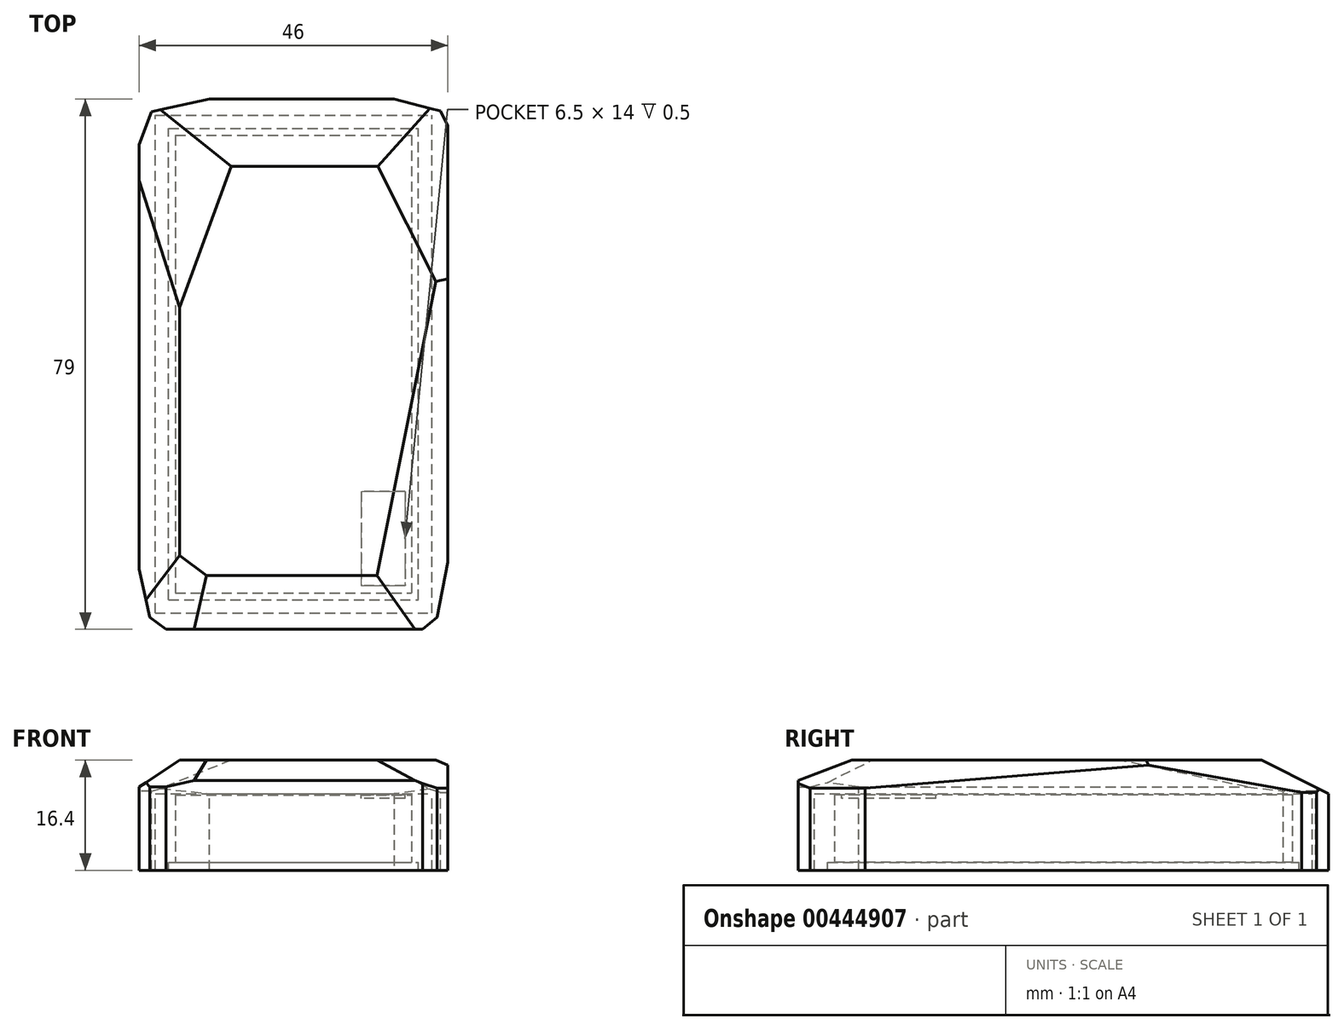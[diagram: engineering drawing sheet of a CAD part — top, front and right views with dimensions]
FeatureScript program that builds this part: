
annotation { "Feature Type Name" : "Feature", "Feature Type Description" : "" }
export const myFeature = defineFeature(function(context is Context, id is Id, definition is map)
    precondition{}
    {
        {
            var Q0;
            Q0=qCreatedBy(makeId("Top.planeOp"),FACE);
            var sketch = newSketch(context, id + "F0", { "sketchPlane" : qUnion([Q0])});
            skLineSegment(sketch, "E0.bottom", {"start": v(-17.6, 34.1) * mm, "end": v(17.6, 34.1) * mm});
            skLineSegment(sketch, "E0.top", {"start": v(-17.6, -34.1) * mm, "end": v(17.6, -34.1) * mm});
            skLineSegment(sketch, "E0.left", {"start": v(-17.6, 34.1) * mm, "end": v(-17.6, -34.1) * mm});
            skLineSegment(sketch, "E0.right", {"start": v(17.6, 34.1) * mm, "end": v(17.6, -34.1) * mm});
            skPoint(sketch, "E0.middle", {"position": v(0, 0) * mm});
            skSolve(sketch);
        }
        {
            var Q0;
            Q0=makeQuery(id+"F0.imprint","IMPRINT",FACE,{"disambiguationData":[TD([[makeQuery(id+"F0.imprint","IMPRINT",EDGE,{"derivedFrom":sQuery(id+"F0.wireOp",EDGE,"E0.bottom")}),-1.0]])]});
            extrude(context, id + "F1", {"entities" : qUnion([Q0]), "depth" : 10 * mm});
        }
        {
            var Q0;
            Q0=makeQuery(id+"F1.opExtrude","CAP_FACE",FACE,{"disambiguationData":[OSD([sQuery(id+"F0.wireOp",EDGE,"E0.bottom"),sQuery(id+"F0.wireOp",EDGE,"E0.top"),sQuery(id+"F0.wireOp",EDGE,"E0.left"),sQuery(id+"F0.wireOp",EDGE,"E0.right")])],"isStart":false});
            var sketch = newSketch(context, id + "F2", { "sketchPlane" : qUnion([Q0])});
            skLineSegment(sketch, "E1.bottom", {"start": v(16.6, -19) * mm, "end": v(10.1, -19) * mm});
            skLineSegment(sketch, "E1.top", {"start": v(16.6, -33) * mm, "end": v(10.1, -33) * mm});
            skLineSegment(sketch, "E1.left", {"start": v(16.6, -19) * mm, "end": v(16.6, -33) * mm});
            skLineSegment(sketch, "E1.right", {"start": v(10.1, -19) * mm, "end": v(10.1, -33) * mm});
            skPoint(sketch, "E1.middle", {"position": v(13.35, -26) * mm});
            skSolve(sketch);
        }
        {
            var Q0;
            Q0=qSketchRegion(id+"F2",true);
            extrude(context, id + "F3", {"entities" : qUnion([Q0]), "operationType" : NewBodyOperationType.REMOVE, "oppositeDirection" : true, "depth" : 0.5 * mm});
        }
        {
            var Q0;
            Q0=makeQuery(id+"F1.opExtrude","CAP_FACE",FACE,{"disambiguationData":[OSD([sQuery(id+"F0.wireOp",EDGE,"E0.bottom"),sQuery(id+"F0.wireOp",EDGE,"E0.top"),sQuery(id+"F0.wireOp",EDGE,"E0.left"),sQuery(id+"F0.wireOp",EDGE,"E0.right")])],"isStart":true});
            var sketch = newSketch(context, id + "F4", { "sketchPlane" : qUnion([Q0])});
            skLineSegment(sketch, "E2.bottom", {"start": v(-18.6, 35.1) * mm, "end": v(18.6, 35.1) * mm});
            skLineSegment(sketch, "E2.top", {"start": v(-18.6, -35.1) * mm, "end": v(18.6, -35.1) * mm});
            skLineSegment(sketch, "E2.left", {"start": v(-18.6, 35.1) * mm, "end": v(-18.6, -35.1) * mm});
            skLineSegment(sketch, "E2.right", {"start": v(18.6, 35.1) * mm, "end": v(18.6, -35.1) * mm});
            skPoint(sketch, "E2.middle", {"position": v(0, 0) * mm});
            skSolve(sketch);
        }
        {
            var Q0;
            Q0=qSketchRegion(id+"F4",true);
            extrude(context, id + "F5", {"entities" : qUnion([Q0]), "depth" : 1.2 * mm});
        }
        {
            var Q0;
            Q0=makeQuery(id+"F1.opExtrude","CAP_FACE",FACE,{"disambiguationData":[OSD([sQuery(id+"F0.wireOp",EDGE,"E0.bottom"),sQuery(id+"F0.wireOp",EDGE,"E0.top"),sQuery(id+"F0.wireOp",EDGE,"E0.left"),sQuery(id+"F0.wireOp",EDGE,"E0.right")])],"isStart":false});
            var sketch = newSketch(context, id + "F6", { "sketchPlane" : qUnion([Q0])});
            skLineSegment(sketch, "E3.0", {"start": v(-20.6, 37.1) * mm, "end": v(20.6, 37.1) * mm});
            skLineSegment(sketch, "E3.1", {"start": v(-20.6, -37.1) * mm, "end": v(-20.6, 37.1) * mm});
            skLineSegment(sketch, "E3.2", {"start": v(-20.6, -37.1) * mm, "end": v(20.6, -37.1) * mm});
            skLineSegment(sketch, "E3.3", {"start": v(20.6, -37.1) * mm, "end": v(20.6, 37.1) * mm});
            skLineSegment(sketch, "E4.0", {"start": v(-23, 39.5) * mm, "end": v(23, 39.5) * mm});
            skLineSegment(sketch, "E4.1", {"start": v(-23, -39.5) * mm, "end": v(-23, 39.5) * mm});
            skLineSegment(sketch, "E4.2", {"start": v(-23, -39.5) * mm, "end": v(23, -39.5) * mm});
            skLineSegment(sketch, "E4.3", {"start": v(23, -39.5) * mm, "end": v(23, 39.5) * mm});
            skSolve(sketch);
        }
        {
            var Q0;
            Q0=qSketchRegion(id+"F6",true);
            var Q1;
            Q1=makeQuery(id+"F5.opExtrude","CAP_FACE",FACE,{"disambiguationData":[OSD([sQuery(id+"F4.wireOp",EDGE,"E2.bottom"),sQuery(id+"F4.wireOp",EDGE,"E2.top"),sQuery(id+"F4.wireOp",EDGE,"E2.left"),sQuery(id+"F4.wireOp",EDGE,"E2.right")])],"isStart":false});
            extrude(context, id + "F7", {"entities" : qUnion([Q0]), "endBound" : BoundingType.UP_TO_SURFACE, "oppositeDirection" : true, "endBoundEntityFace" : qUnion([Q1]), "depth" : 25 * mm, "hasSecondDirection" : true, "secondDirectionOppositeDirection" : false, "secondDirectionDepth" : 0.2 * mm});
        }
        {
            var Q0;
            Q0=makeQuery(id+"F7.opExtrude","CAP_FACE",FACE,{"disambiguationData":[OSD([sQuery(id+"F6.wireOp",EDGE,"E3.0"),sQuery(id+"F6.wireOp",EDGE,"E3.1"),sQuery(id+"F6.wireOp",EDGE,"E3.2"),sQuery(id+"F6.wireOp",EDGE,"E3.3"),sQuery(id+"F6.wireOp",EDGE,"E4.0"),sQuery(id+"F6.wireOp",EDGE,"E4.1"),sQuery(id+"F6.wireOp",EDGE,"E4.2"),sQuery(id+"F6.wireOp",EDGE,"E4.3")])],"isStart":true});
            var sketch = newSketch(context, id + "F8", { "sketchPlane" : qUnion([Q0])});
            skLineSegment(sketch, "E5.0.0", {"start": v(-23, -39.5) * mm, "end": v(23, -39.5) * mm});
            skLineSegment(sketch, "E5.0.1", {"start": v(23, -39.5) * mm, "end": v(23, 39.5) * mm});
            skLineSegment(sketch, "E5.0.2", {"start": v(23, 39.5) * mm, "end": v(-23, 39.5) * mm});
            skLineSegment(sketch, "E5.0.3", {"start": v(-23, 39.5) * mm, "end": v(-23, -39.5) * mm});
            skSolve(sketch);
        }
        {
            var Q0;
            Q0=qSketchRegion(id+"F8",true);
            extrude(context, id + "F9", {"entities" : qUnion([Q0]), "operationType" : NewBodyOperationType.ADD, "depth" : 5 * mm});
        }
        {
            var Q0;
            Q0=makeQuery(id+"F9.boolean.opBoolean","MERGE",EDGE,{"derivedFrom":[makeQuery(id+"F7.opExtrude","SWEPT_EDGE",EDGE,{"disambiguationData":[OSD([sQuery(id+"F6.wireOp",EDGE,"E4.2"),sQuery(id+"F6.wireOp",EDGE,"E4.3")])]}),makeQuery(id+"F9.opExtrude","SWEPT_EDGE",EDGE,{"disambiguationData":[OSD([sQuery(id+"F8.wireOp",EDGE,"E5.0.0"),sQuery(id+"F8.wireOp",EDGE,"E5.0.1")])]})]});
            chamfer(context, id + "F10", {"entities" : qUnion([Q0]), "chamferType" : ChamferType.TWO_OFFSETS, "width1" : 2 * mm, "oppositeDirection" : false, "width2" : 10 * mm, "tangentPropagation" : true});
        }
        {
            var Q0;
            Q0=makeQuery(id+"F9.boolean.opBoolean","MERGE",EDGE,{"derivedFrom":[makeQuery(id+"F7.opExtrude","SWEPT_EDGE",EDGE,{"disambiguationData":[OSD([sQuery(id+"F6.wireOp",EDGE,"E4.1"),sQuery(id+"F6.wireOp",EDGE,"E4.2")])]}),makeQuery(id+"F9.opExtrude","SWEPT_EDGE",EDGE,{"disambiguationData":[OSD([sQuery(id+"F8.wireOp",EDGE,"E5.0.0"),sQuery(id+"F8.wireOp",EDGE,"E5.0.3")])]})]});
            chamfer(context, id + "F11", {"entities" : qUnion([Q0]), "chamferType" : ChamferType.TWO_OFFSETS, "width1" : 3 * mm, "oppositeDirection" : false, "width2" : 4 * mm, "tangentPropagation" : true});
        }
        {
            var Q0;
            Q0=makeQuery(id+"F9.boolean.opBoolean","MERGE",EDGE,{"derivedFrom":[makeQuery(id+"F7.opExtrude","SWEPT_EDGE",EDGE,{"disambiguationData":[OSD([sQuery(id+"F6.wireOp",EDGE,"E4.0"),sQuery(id+"F6.wireOp",EDGE,"E4.1")])]}),makeQuery(id+"F9.opExtrude","SWEPT_EDGE",EDGE,{"disambiguationData":[OSD([sQuery(id+"F8.wireOp",EDGE,"E5.0.2"),sQuery(id+"F8.wireOp",EDGE,"E5.0.3")])]})]});
            chamfer(context, id + "F12", {"entities" : qUnion([Q0]), "chamferType" : ChamferType.TWO_OFFSETS, "width1" : 2.5 * mm, "oppositeDirection" : false, "width2" : 6.8 * mm, "tangentPropagation" : true});
        }
        {
            var Q0;
            Q0=makeQuery(id+"F9.boolean.opBoolean","MERGE",EDGE,{"derivedFrom":[makeQuery(id+"F7.opExtrude","SWEPT_EDGE",EDGE,{"disambiguationData":[OSD([sQuery(id+"F6.wireOp",EDGE,"E4.0"),sQuery(id+"F6.wireOp",EDGE,"E4.3")])]}),makeQuery(id+"F9.opExtrude","SWEPT_EDGE",EDGE,{"disambiguationData":[OSD([sQuery(id+"F8.wireOp",EDGE,"E5.0.1"),sQuery(id+"F8.wireOp",EDGE,"E5.0.2")])]})]});
            chamfer(context, id + "F13", {"entities" : qUnion([Q0]), "chamferType" : ChamferType.TWO_OFFSETS, "width1" : 4 * mm, "oppositeDirection" : false, "width2" : 2 * mm, "tangentPropagation" : true});
        }
        {
            var Q0;
            {var subQ0=sQuery(id+"F8.wireOp",EDGE,"E5.0.3");var subQ1=sQuery(id+"F8.wireOp",EDGE,"E5.0.2");Q0=makeQuery(id+"F12.opChamfer","BLEND_EDGE",EDGE,{"blendedFrom":[makeQuery(id+"F9.boolean.opBoolean","MERGE",EDGE,{"derivedFrom":[makeQuery(id+"F7.opExtrude","SWEPT_EDGE",EDGE,{"disambiguationData":[OSD([sQuery(id+"F6.wireOp",EDGE,"E4.0"),sQuery(id+"F6.wireOp",EDGE,"E4.1")])]}),makeQuery(id+"F9.opExtrude","SWEPT_EDGE",EDGE,{"disambiguationData":[OSD([subQ1,subQ0])]})]}),makeQuery(id+"F9.opExtrude","CAP_FACE",FACE,{"disambiguationData":[OSD([sQuery(id+"F8.wireOp",EDGE,"E5.0.0"),sQuery(id+"F8.wireOp",EDGE,"E5.0.1"),subQ1,subQ0])],"isStart":false})],"blendedInto":[makeQuery(id+"F9.opExtrude","CAP_FACE",FACE,{"disambiguationData":[OSD([sQuery(id+"F8.wireOp",EDGE,"E5.0.0"),sQuery(id+"F8.wireOp",EDGE,"E5.0.1"),subQ1,subQ0])],"isStart":false})]});}
            chamfer(context, id + "F14", {"entities" : qUnion([Q0]), "chamferType" : ChamferType.TWO_OFFSETS, "width1" : 14 * mm, "oppositeDirection" : false, "width2" : 4.6 * mm, "tangentPropagation" : true});
        }
        {
            var Q0;
            {var subQ0=sQuery(id+"F8.wireOp",EDGE,"E5.0.3");var subQ1=sQuery(id+"F8.wireOp",EDGE,"E5.0.0");Q0=makeQuery(id+"F11.opChamfer","BLEND_EDGE",EDGE,{"blendedFrom":[makeQuery(id+"F9.boolean.opBoolean","MERGE",EDGE,{"derivedFrom":[makeQuery(id+"F7.opExtrude","SWEPT_EDGE",EDGE,{"disambiguationData":[OSD([sQuery(id+"F6.wireOp",EDGE,"E4.1"),sQuery(id+"F6.wireOp",EDGE,"E4.2")])]}),makeQuery(id+"F9.opExtrude","SWEPT_EDGE",EDGE,{"disambiguationData":[OSD([subQ1,subQ0])]})]}),makeQuery(id+"F9.opExtrude","CAP_FACE",FACE,{"disambiguationData":[OSD([subQ1,sQuery(id+"F8.wireOp",EDGE,"E5.0.1"),sQuery(id+"F8.wireOp",EDGE,"E5.0.2"),subQ0])],"isStart":false})],"blendedInto":[makeQuery(id+"F9.opExtrude","CAP_FACE",FACE,{"disambiguationData":[OSD([subQ1,sQuery(id+"F8.wireOp",EDGE,"E5.0.1"),sQuery(id+"F8.wireOp",EDGE,"E5.0.2"),subQ0])],"isStart":false})]});}
            chamfer(context, id + "F15", {"entities" : qUnion([Q0]), "chamferType" : ChamferType.TWO_OFFSETS, "width1" : 10 * mm, "oppositeDirection" : false, "width2" : 4 * mm, "tangentPropagation" : true});
        }
        {
            var Q0;
            {var subQ0=sQuery(id+"F8.wireOp",EDGE,"E5.0.1");var subQ1=sQuery(id+"F8.wireOp",EDGE,"E5.0.0");Q0=makeQuery(id+"F10.opChamfer","BLEND_EDGE",EDGE,{"blendedFrom":[makeQuery(id+"F9.boolean.opBoolean","MERGE",EDGE,{"derivedFrom":[makeQuery(id+"F7.opExtrude","SWEPT_EDGE",EDGE,{"disambiguationData":[OSD([sQuery(id+"F6.wireOp",EDGE,"E4.2"),sQuery(id+"F6.wireOp",EDGE,"E4.3")])]}),makeQuery(id+"F9.opExtrude","SWEPT_EDGE",EDGE,{"disambiguationData":[OSD([subQ1,subQ0])]})]}),makeQuery(id+"F9.opExtrude","CAP_FACE",FACE,{"disambiguationData":[OSD([subQ1,subQ0,sQuery(id+"F8.wireOp",EDGE,"E5.0.2"),sQuery(id+"F8.wireOp",EDGE,"E5.0.3")])],"isStart":false})],"blendedInto":[makeQuery(id+"F9.opExtrude","CAP_FACE",FACE,{"disambiguationData":[OSD([subQ1,subQ0,sQuery(id+"F8.wireOp",EDGE,"E5.0.2"),sQuery(id+"F8.wireOp",EDGE,"E5.0.3")])],"isStart":false})]});}
            chamfer(context, id + "F16", {"entities" : qUnion([Q0]), "chamferType" : ChamferType.TWO_OFFSETS, "width1" : 10 * mm, "oppositeDirection" : false, "width2" : 4.2 * mm, "tangentPropagation" : true});
        }
        {
            var Q0;
            {var subQ0=sQuery(id+"F8.wireOp",EDGE,"E5.0.2");var subQ1=sQuery(id+"F8.wireOp",EDGE,"E5.0.1");Q0=makeQuery(id+"F13.opChamfer","BLEND_EDGE",EDGE,{"blendedFrom":[makeQuery(id+"F9.boolean.opBoolean","MERGE",EDGE,{"derivedFrom":[makeQuery(id+"F7.opExtrude","SWEPT_EDGE",EDGE,{"disambiguationData":[OSD([sQuery(id+"F6.wireOp",EDGE,"E4.0"),sQuery(id+"F6.wireOp",EDGE,"E4.3")])]}),makeQuery(id+"F9.opExtrude","SWEPT_EDGE",EDGE,{"disambiguationData":[OSD([subQ1,subQ0])]})]}),makeQuery(id+"F9.opExtrude","CAP_FACE",FACE,{"disambiguationData":[OSD([sQuery(id+"F8.wireOp",EDGE,"E5.0.0"),subQ1,subQ0,sQuery(id+"F8.wireOp",EDGE,"E5.0.3")])],"isStart":false})],"blendedInto":[makeQuery(id+"F9.opExtrude","CAP_FACE",FACE,{"disambiguationData":[OSD([sQuery(id+"F8.wireOp",EDGE,"E5.0.0"),subQ1,subQ0,sQuery(id+"F8.wireOp",EDGE,"E5.0.3")])],"isStart":false})]});}
            chamfer(context, id + "F17", {"entities" : qUnion([Q0]), "chamferType" : ChamferType.TWO_OFFSETS, "width1" : 12 * mm, "oppositeDirection" : false, "width2" : 4.8 * mm, "tangentPropagation" : true});
        }
        {
            var Q0;
            Q0=makeQuery(id+"F9.opExtrude","CAP_EDGE",EDGE,{"disambiguationData":[OSD([sQuery(id+"F8.wireOp",EDGE,"E5.0.2")])],"isStart":false});
            chamfer(context, id + "F18", {"entities" : qUnion([Q0]), "chamferType" : ChamferType.TWO_OFFSETS, "width1" : 5 * mm, "oppositeDirection" : false, "width2" : 10 * mm, "tangentPropagation" : true});
        }
        {
            var Q0;
            Q0=makeQuery(id+"F9.opExtrude","CAP_EDGE",EDGE,{"disambiguationData":[OSD([sQuery(id+"F8.wireOp",EDGE,"E5.0.3")])],"isStart":false});
            chamfer(context, id + "F19", {"entities" : qUnion([Q0]), "chamferType" : ChamferType.TWO_OFFSETS, "width1" : 4 * mm, "oppositeDirection" : false, "width2" : 6 * mm, "tangentPropagation" : true});
        }
        {
            var Q0;
            Q0=makeQuery(id+"F9.opExtrude","CAP_EDGE",EDGE,{"disambiguationData":[OSD([sQuery(id+"F8.wireOp",EDGE,"E5.0.0")])],"isStart":false});
            chamfer(context, id + "F20", {"entities" : qUnion([Q0]), "chamferType" : ChamferType.TWO_OFFSETS, "width1" : 8 * mm, "oppositeDirection" : false, "width2" : 3 * mm, "tangentPropagation" : true});
        }
        {
            var Q0;
            {var subQ0=sQuery(id+"F8.wireOp",EDGE,"E5.0.0");var subQ1=sQuery(id+"F6.wireOp",EDGE,"E4.2");Q0=makeQuery(id+"F10.opChamfer","BLEND_EDGE",EDGE,{"blendedFrom":[makeQuery(id+"F9.boolean.opBoolean","MERGE",EDGE,{"derivedFrom":[makeQuery(id+"F7.opExtrude","SWEPT_EDGE",EDGE,{"disambiguationData":[OSD([subQ1,sQuery(id+"F6.wireOp",EDGE,"E4.3")])]}),makeQuery(id+"F9.opExtrude","SWEPT_EDGE",EDGE,{"disambiguationData":[OSD([subQ0,sQuery(id+"F8.wireOp",EDGE,"E5.0.1")])]})]}),makeQuery(id+"F9.boolean.opBoolean","MERGE",FACE,{"derivedFrom":[makeQuery(id+"F7.opExtrude","SWEPT_FACE",FACE,{"disambiguationData":[OSD([subQ1])]}),makeQuery(id+"F9.opExtrude","SWEPT_FACE",FACE,{"disambiguationData":[OSD([subQ0])]})]})],"blendedInto":[makeQuery(id+"F9.boolean.opBoolean","MERGE",FACE,{"derivedFrom":[makeQuery(id+"F7.opExtrude","SWEPT_FACE",FACE,{"disambiguationData":[OSD([subQ1])]}),makeQuery(id+"F9.opExtrude","SWEPT_FACE",FACE,{"disambiguationData":[OSD([subQ0])]})]})]});}
            chamfer(context, id + "F21", {"entities" : qUnion([Q0]), "width" : 2.2 * mm, "tangentPropagation" : true});
        }
        {
            var Q0;
            {var subQ0=sQuery(id+"F8.wireOp",EDGE,"E5.0.2");var subQ1=sQuery(id+"F6.wireOp",EDGE,"E4.0");Q0=makeQuery(id+"F12.opChamfer","BLEND_EDGE",EDGE,{"blendedFrom":[makeQuery(id+"F9.boolean.opBoolean","MERGE",EDGE,{"derivedFrom":[makeQuery(id+"F7.opExtrude","SWEPT_EDGE",EDGE,{"disambiguationData":[OSD([subQ1,sQuery(id+"F6.wireOp",EDGE,"E4.1")])]}),makeQuery(id+"F9.opExtrude","SWEPT_EDGE",EDGE,{"disambiguationData":[OSD([subQ0,sQuery(id+"F8.wireOp",EDGE,"E5.0.3")])]})]}),makeQuery(id+"F9.boolean.opBoolean","MERGE",FACE,{"derivedFrom":[makeQuery(id+"F7.opExtrude","SWEPT_FACE",FACE,{"disambiguationData":[OSD([subQ1])]}),makeQuery(id+"F9.opExtrude","SWEPT_FACE",FACE,{"disambiguationData":[OSD([subQ0])]})]})],"blendedInto":[makeQuery(id+"F9.boolean.opBoolean","MERGE",FACE,{"derivedFrom":[makeQuery(id+"F7.opExtrude","SWEPT_FACE",FACE,{"disambiguationData":[OSD([subQ1])]}),makeQuery(id+"F9.opExtrude","SWEPT_FACE",FACE,{"disambiguationData":[OSD([subQ0])]})]})]});}
            chamfer(context, id + "F22", {"entities" : qUnion([Q0]), "chamferType" : ChamferType.TWO_OFFSETS, "width1" : 8 * mm, "oppositeDirection" : false, "width2" : 2 * mm, "tangentPropagation" : true});
        }
        {
            var Q0;
            {var subQ0=sQuery(id+"F8.wireOp",EDGE,"E5.0.2");var subQ1=sQuery(id+"F6.wireOp",EDGE,"E4.0");Q0=makeQuery(id+"F13.opChamfer","BLEND_EDGE",EDGE,{"blendedFrom":[makeQuery(id+"F9.boolean.opBoolean","MERGE",EDGE,{"derivedFrom":[makeQuery(id+"F7.opExtrude","SWEPT_EDGE",EDGE,{"disambiguationData":[OSD([subQ1,sQuery(id+"F6.wireOp",EDGE,"E4.3")])]}),makeQuery(id+"F9.opExtrude","SWEPT_EDGE",EDGE,{"disambiguationData":[OSD([sQuery(id+"F8.wireOp",EDGE,"E5.0.1"),subQ0])]})]}),makeQuery(id+"F9.boolean.opBoolean","MERGE",FACE,{"derivedFrom":[makeQuery(id+"F7.opExtrude","SWEPT_FACE",FACE,{"disambiguationData":[OSD([subQ1])]}),makeQuery(id+"F9.opExtrude","SWEPT_FACE",FACE,{"disambiguationData":[OSD([subQ0])]})]})],"blendedInto":[makeQuery(id+"F9.boolean.opBoolean","MERGE",FACE,{"derivedFrom":[makeQuery(id+"F7.opExtrude","SWEPT_FACE",FACE,{"disambiguationData":[OSD([subQ1])]}),makeQuery(id+"F9.opExtrude","SWEPT_FACE",FACE,{"disambiguationData":[OSD([subQ0])]})]})]});}
            chamfer(context, id + "F23", {"entities" : qUnion([Q0]), "chamferType" : ChamferType.TWO_OFFSETS, "width1" : 6 * mm, "oppositeDirection" : false, "width2" : 2 * mm, "tangentPropagation" : true});
        }
        {
            var Q0;
            {var subQ0=sQuery(id+"F8.wireOp",EDGE,"E5.0.3");var subQ1=sQuery(id+"F6.wireOp",EDGE,"E4.1");Q0=makeQuery(id+"F11.opChamfer","BLEND_EDGE",EDGE,{"blendedFrom":[makeQuery(id+"F9.boolean.opBoolean","MERGE",EDGE,{"derivedFrom":[makeQuery(id+"F7.opExtrude","SWEPT_EDGE",EDGE,{"disambiguationData":[OSD([subQ1,sQuery(id+"F6.wireOp",EDGE,"E4.2")])]}),makeQuery(id+"F9.opExtrude","SWEPT_EDGE",EDGE,{"disambiguationData":[OSD([sQuery(id+"F8.wireOp",EDGE,"E5.0.0"),subQ0])]})]}),makeQuery(id+"F9.boolean.opBoolean","MERGE",FACE,{"derivedFrom":[makeQuery(id+"F7.opExtrude","SWEPT_FACE",FACE,{"disambiguationData":[OSD([subQ1])]}),makeQuery(id+"F9.opExtrude","SWEPT_FACE",FACE,{"disambiguationData":[OSD([subQ0])]})]})],"blendedInto":[makeQuery(id+"F9.boolean.opBoolean","MERGE",FACE,{"derivedFrom":[makeQuery(id+"F7.opExtrude","SWEPT_FACE",FACE,{"disambiguationData":[OSD([subQ1])]}),makeQuery(id+"F9.opExtrude","SWEPT_FACE",FACE,{"disambiguationData":[OSD([subQ0])]})]})]});}
            chamfer(context, id + "F24", {"entities" : qUnion([Q0]), "chamferType" : ChamferType.TWO_OFFSETS, "width1" : 6 * mm, "oppositeDirection" : false, "width2" : 2 * mm, "tangentPropagation" : true});
        }
    });
